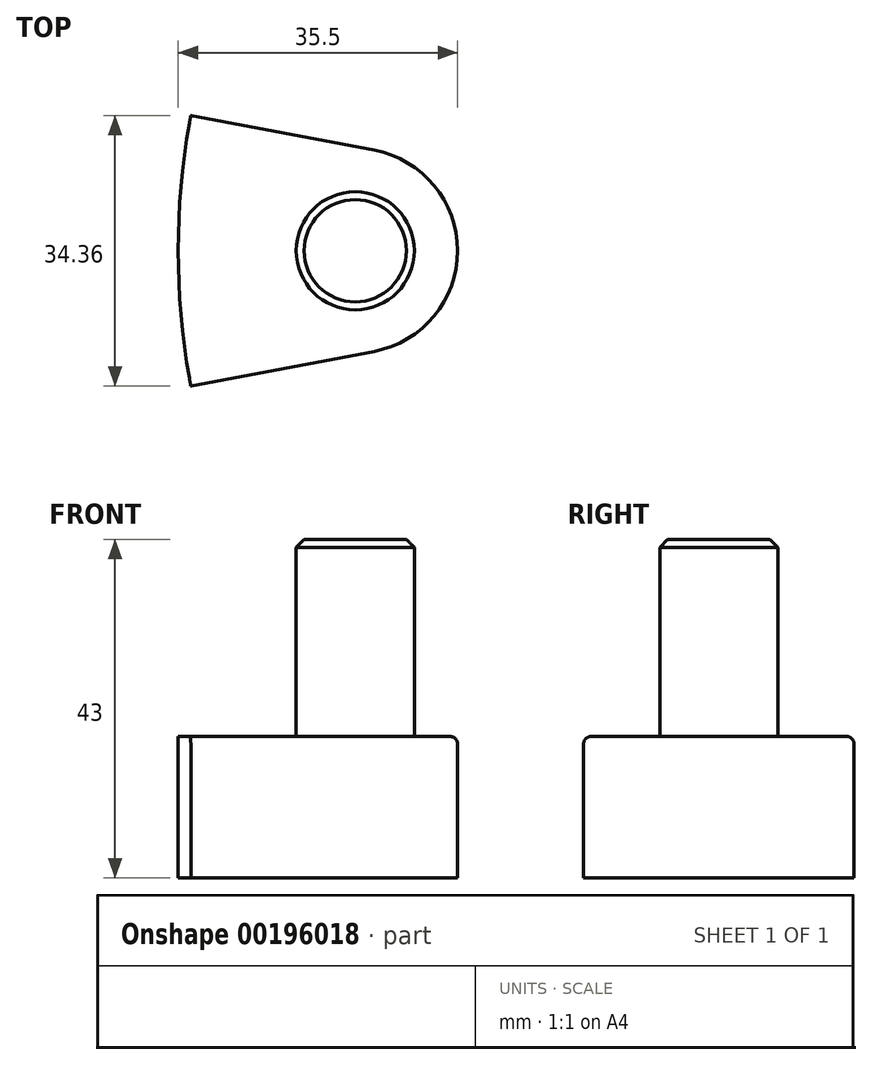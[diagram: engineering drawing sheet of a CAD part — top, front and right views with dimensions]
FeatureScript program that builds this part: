
annotation { "Feature Type Name" : "Feature", "Feature Type Description" : "" }
export const myFeature = defineFeature(function(context is Context, id is Id, definition is map)
    precondition{}
    {
        {
            var Q0;
            Q0=qCreatedBy(makeId("Top.planeOp"),FACE);
            var sketch = newSketch(context, id + "F0", { "sketchPlane" : qUnion([Q0])});
            skArc(sketch, "E0", {"start": v(-90.9, 17.18) * mm, "mid": v(-92.5, 0) * mm, "end": v(-90.9, -17.18) * mm});
            skArc(sketch, "E1", {"start": v(-67.59, -12.77) * mm, "mid": v(-57, 0) * mm, "end": v(-67.59, 12.77) * mm});
            skLineSegment(sketch, "E2", {"start": v(-67.59, 12.77) * mm, "end": v(-90.9, 17.18) * mm});
            skLineSegment(sketch, "E3", {"start": v(-67.59, -12.77) * mm, "end": v(-90.9, -17.18) * mm});
            skPoint(sketch, "E4.start.orphan", {"position": v(-55.08, 0) * mm});
            skSolve(sketch);
        }
        {
            var Q0;
            Q0 = qSketchRegion(id + "F0", true);
            extrude(context, id + "F1", {"entities" : qUnion([Q0]), "depth" : 18 * mm});
        }
        {
            var Q0;
            Q0=makeQuery(id+"F1.opExtrude","CAP_FACE",FACE,{"disambiguationData":[OSD([sQuery(id+"F0.wireOp",EDGE,"E0"),sQuery(id+"F0.wireOp",EDGE,"E1"),sQuery(id+"F0.wireOp",EDGE,"E2"),sQuery(id+"F0.wireOp",EDGE,"E3")])],"isStart":false});
            var sketch = newSketch(context, id + "F2", { "sketchPlane" : qUnion([Q0])});
            skCircle(sketch, "E5", {"center": v(-70, 0) * mm, "radius": 7.5 * mm});
            skSolve(sketch);
        }
        {
            var Q0;
            Q0=makeQuery(id+"F2.imprint","IMPRINT",FACE,{"disambiguationData":[TD([[makeQuery(id+"F2.imprint","IMPRINT",EDGE,{"derivedFrom":sQuery(id+"F2.wireOp",EDGE,"E5")}),1.0]])]});
            extrude(context, id + "F3", {"entities" : qUnion([Q0]), "operationType" : NewBodyOperationType.ADD, "depth" : 25 * mm});
        }
        {
            var Q0;
            Q0=makeQuery(id+"F3.opExtrude","CAP_EDGE",EDGE,{"disambiguationData":[OSD([sQuery(id+"F2.wireOp",EDGE,"E5")])],"isStart":true});
            var Q1;
            Q1=makeQuery(id+"F1.opExtrude","CAP_EDGE",EDGE,{"disambiguationData":[OSD([sQuery(id+"F0.wireOp",EDGE,"E2")])],"isStart":false});
            fillet(context, id + "F4", {"entities" : qUnion([Q0, Q1]), "radius" : 1 * mm, "tangentPropagation" : true, "allowEdgeOverflow" : false});
        }
        {
            var Q0;
            Q0=makeQuery(id+"F3.opExtrude","CAP_EDGE",EDGE,{"disambiguationData":[OSD([sQuery(id+"F2.wireOp",EDGE,"E5")])],"isStart":false});
            chamfer(context, id + "F5", {"entities" : qUnion([Q0]), "width" : 1 * mm, "tangentPropagation" : true});
        }
    });
